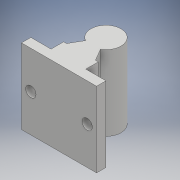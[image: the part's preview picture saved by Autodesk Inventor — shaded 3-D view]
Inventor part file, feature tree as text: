
AUTODESK INVENTOR PART (.ipt)
format: ipt  version: 2018 (Build 220112000, 112)  size: 131,584 bytes
history: native  units: mm
features: sketch x2, other x1, extrude x1, hole x1
ambient origin geometry x8: Origin, YZ Plane, XZ Plane, XY Plane, X Axis, Y Axis, Z Axis, Center Point
bodies: Body1 (feature_tree)
feature tree (5):
  other  "Sólido1"
  extrude  "Extrusão1"  Depth=25.0mm
  hole  "Furo1"  [1 undecoded]
  sketch  "Esboço1"  dims[d6=16.0mm d7=25.0mm]
  sketch  "Esboço3"  dims[d8=18.5mm d9=11.7mm d10=8.0mm d11=30.0deg d12=30.0deg d13=5.0mm d14=40.0mm d15=40.0mm d16=0.0mm d18=15.0mm d19=15.0mm d20=5.5mm d21=5.5mm d22=20.0mm d28=5.5mm d29=6.0mm d30=4.0mm d31=2.0mm d32=90.0deg d33=8.0mm d34=20.594885mm]
note: 1 required parameter value undecoded (feature->parameter linkage not recoverable at this tier; creation-order binding heuristic only, values carry confidence <= 0.55)
